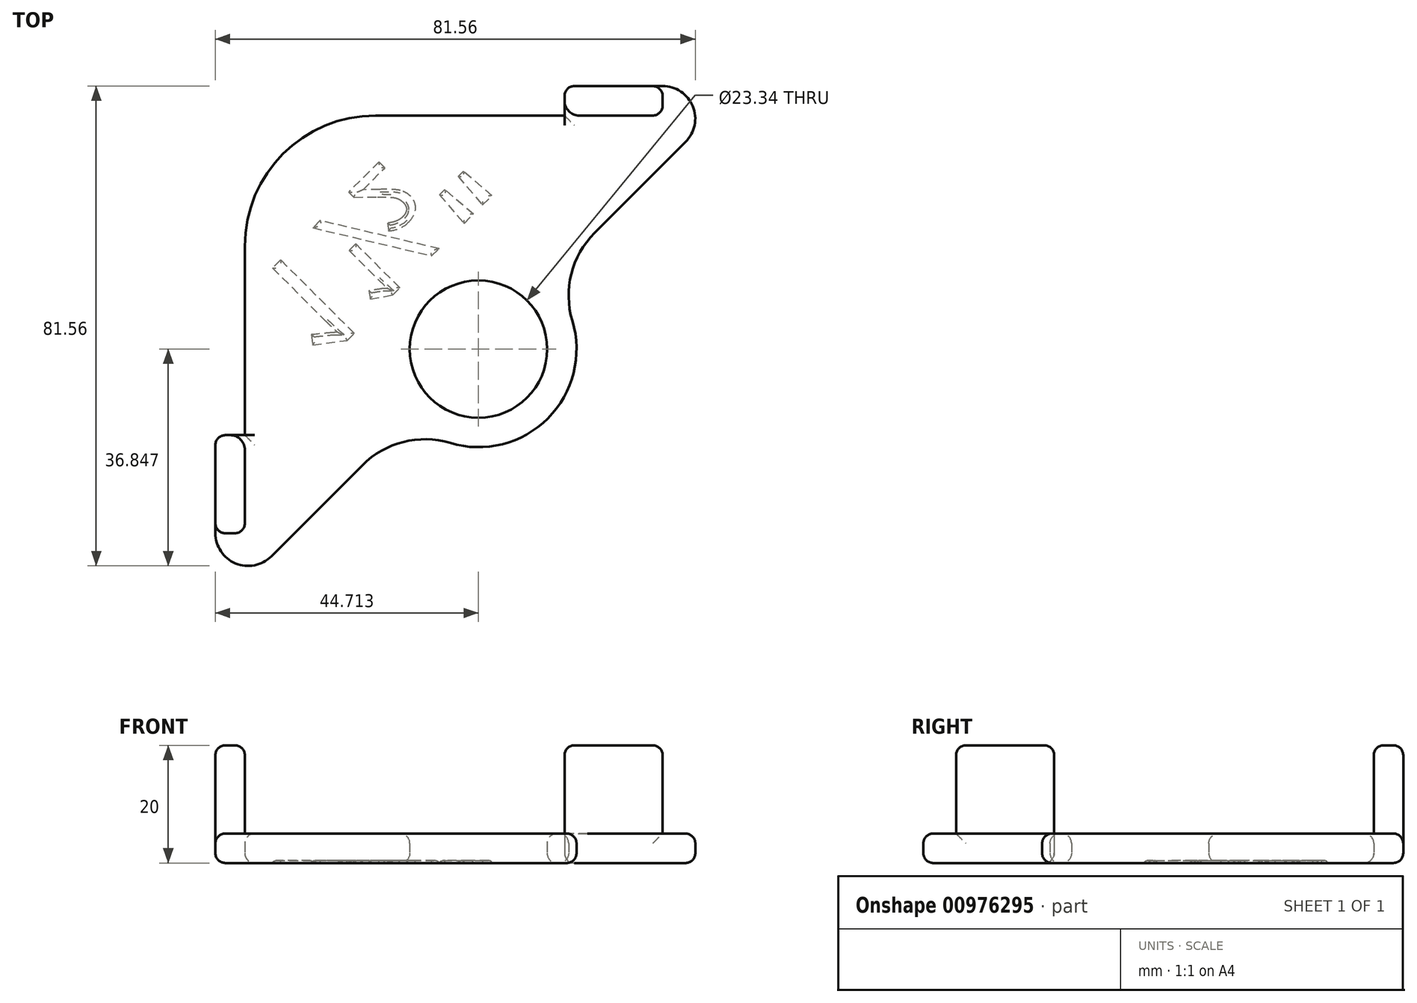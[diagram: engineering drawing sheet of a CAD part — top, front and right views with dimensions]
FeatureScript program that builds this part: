
annotation { "Feature Type Name" : "Feature", "Feature Type Description" : "" }
export const myFeature = defineFeature(function(context is Context, id is Id, definition is map)
    precondition{}
    {
        {
            assignVariable(context, id + "F0", {"name" : "t", "anyValue" : 5});
        }
        {
            var Q0;
            Q0=qCreatedBy(makeId("Top.planeOp"),FACE);
            var sketch = newSketch(context, id + "F1", { "sketchPlane" : qUnion([Q0])});
            skLineSegment(sketch, "E0", {"start": v(-22.22, 0) * mm, "end": v(-22.22, -48.78) * mm});
            skLineSegment(sketch, "E1", {"start": v(0, 22.22) * mm, "end": v(48.78, 22.22) * mm});
            skLineSegment(sketch, "E2", {"start": v(52.7, 17.74) * mm, "end": v(29.27, -5.7) * mm});
            skLineSegment(sketch, "E3.bottom", {"start": v(-22.22, -32.1) * mm, "end": v(-27.22, -32.1) * mm});
            skLineSegment(sketch, "E3.top", {"start": v(-22.22, -48.78) * mm, "end": v(-27.22, -48.78) * mm});
            skLineSegment(sketch, "E3.left", {"start": v(-22.22, -32.1) * mm, "end": v(-22.22, -48.78) * mm});
            skLineSegment(sketch, "E3.right", {"start": v(-27.22, -32.1) * mm, "end": v(-27.22, -48.78) * mm});
            skLineSegment(sketch, "E4.bottom", {"start": v(32.1, 22.22) * mm, "end": v(48.78, 22.22) * mm});
            skLineSegment(sketch, "E4.top", {"start": v(32.1, 27.22) * mm, "end": v(48.78, 27.22) * mm});
            skLineSegment(sketch, "E4.left", {"start": v(32.1, 22.22) * mm, "end": v(32.1, 27.22) * mm});
            skLineSegment(sketch, "E4.right", {"start": v(48.78, 22.22) * mm, "end": v(48.78, 27.22) * mm});
            skCircle(sketch, "E5", {"center": v(17.48, -17.48) * mm, "radius": 11.67 * mm});
            skArc(sketch, "E6", {"start": v(0, 22.22) * mm, "mid": v(-15.72, 15.72) * mm, "end": v(-22.22, 0) * mm});
            skArc(sketch, "E7", {"start": v(-22.22, 0) * mm, "mid": v(15.72, -15.72) * mm, "end": v(0, 22.22) * mm, "construction": true});
            skArc(sketch, "E8", {"start": v(29.27, -5.7) * mm, "mid": v(5.7, -5.7) * mm, "end": v(5.7, -29.27) * mm, "construction": true});
            skArc(sketch, "E9", {"start": v(5.7, -29.27) * mm, "mid": v(29.27, -29.27) * mm, "end": v(29.27, -5.7) * mm});
            skArc(sketch, "E10", {"start": v(48.78, 27.23) * mm, "mid": v(43.64, 19.54) * mm, "end": v(52.7, 17.74) * mm, "construction": true});
            skArc(sketch, "E11", {"start": v(52.7, 17.74) * mm, "mid": v(53.91, 23.8) * mm, "end": v(48.78, 27.23) * mm});
            skArc(sketch, "E12", {"start": v(-27.23, -48.78) * mm, "mid": v(-23.8, -53.91) * mm, "end": v(-17.74, -52.7) * mm});
            skArc(sketch, "E13", {"start": v(-17.74, -52.7) * mm, "mid": v(-19.54, -43.64) * mm, "end": v(-27.23, -48.78) * mm, "construction": true});
            skLineSegment(sketch, "E14", {"start": v(29.27, -5.7) * mm, "end": v(5.7, -29.27) * mm, "construction": true});
            skLineSegment(sketch, "E15", {"start": v(5.7, -29.27) * mm, "end": v(-17.74, -52.7) * mm});
            skSolve(sketch);
        }
        {
            var Q0;
            Q0=makeQuery(id+"F1.imprint","IMPRINT",FACE,{"disambiguationData":[TD([[makeQuery(id+"F1.imprint","IMPRINT",EDGE,{"derivedFrom":sQuery(id+"F1.wireOp",EDGE,"Bsdqljn9-m8OD-Z169-KwQe-wA3pNiIeevgB")}),1.0]])]});
            var Q1;
            Q1=makeQuery(id+"F1.imprint","IMPRINT",FACE,{"disambiguationData":[TD([[makeQuery(id+"F1.imprint","IMPRINT",EDGE,{"derivedFrom":sQuery(id+"F1.wireOp",EDGE,"E2")}),-1.0]])]});
            var Q2;
            Q2=makeQuery(id+"F1.imprint","IMPRINT",FACE,{"disambiguationData":[TD([[makeQuery(id+"F1.imprint","IMPRINT",EDGE,{"derivedFrom":sQuery(id+"F1.wireOp",EDGE,"E2")}),-1.0]])]});
            var Q3;
            {var subQ0=sQuery(id+"F1.wireOp",EDGE,"1yZtRJ6P-QjRJ-GIre-H2JQ-c21tXZH1Mfqz");var subQ1=makeQuery(id+"F1.imprint","INTERSECT",VERTEX,{"derivedFrom":[subQ0,sQuery(id+"F1.wireOp",EDGE,"E0")]});Q3=makeQuery(id+"F1.imprint","IMPRINT",FACE,{"disambiguationData":[TD([[makeQuery(id+"F1.imprint","IMPRINT",EDGE,{"disambiguationData":[TD([[subQ1,1.0]])],"derivedFrom":subQ0}),1.0]])]});}
            var Q4;
            {var subQ0=sQuery(id+"F1.wireOp",EDGE,"sP8yukeB-kcOP-x4iM-DJbK-dVnLuw5eq7dv");var subQ1=sQuery(id+"F1.wireOp",EDGE,"1yZtRJ6P-QjRJ-GIre-H2JQ-c21tXZH1Mfqz");var subQ2=makeQuery(id+"F1.imprint","INTERSECT",VERTEX,{"disambiguationData":[OD(0.0)],"derivedFrom":[subQ1,subQ0]});Q4=makeQuery(id+"F1.imprint","IMPRINT",FACE,{"disambiguationData":[TD([[makeQuery(id+"F1.imprint","IMPRINT",EDGE,{"disambiguationData":[TD([[subQ2,-1.0]])],"derivedFrom":subQ1}),1.0]])]});}
            var Q5;
            {var subQ0=sQuery(id+"F1.wireOp",EDGE,"sP8yukeB-kcOP-x4iM-DJbK-dVnLuw5eq7dv");var subQ1=sQuery(id+"F1.wireOp",EDGE,"1yZtRJ6P-QjRJ-GIre-H2JQ-c21tXZH1Mfqz");var subQ2=makeQuery(id+"F1.imprint","INTERSECT",VERTEX,{"disambiguationData":[OD(0.0)],"derivedFrom":[subQ1,subQ0]});Q5=makeQuery(id+"F1.imprint","IMPRINT",FACE,{"disambiguationData":[TD([[makeQuery(id+"F1.imprint","IMPRINT",EDGE,{"disambiguationData":[TD([[subQ2,-1.0]])],"derivedFrom":subQ1}),-1.0]])]});}
            var Q6;
            {var subQ0=sQuery(id+"F1.wireOp",EDGE,"E2");var subQ1=sQuery(id+"F1.wireOp",EDGE,"1yZtRJ6P-QjRJ-GIre-H2JQ-c21tXZH1Mfqz");var subQ2=makeQuery(id+"F1.imprint","INTERSECT",VERTEX,{"disambiguationData":[OD(1.0)],"derivedFrom":[subQ1,subQ0]});Q6=makeQuery(id+"F1.imprint","IMPRINT",FACE,{"disambiguationData":[TD([[makeQuery(id+"F1.imprint","IMPRINT",EDGE,{"disambiguationData":[TD([[subQ2,-1.0]])],"derivedFrom":subQ1}),-1.0]])]});}
            var Q7;
            Q7=makeQuery(id+"F1.imprint","IMPRINT",FACE,{"disambiguationData":[TD([[makeQuery(id+"F1.imprint","IMPRINT",EDGE,{"derivedFrom":sQuery(id+"F1.wireOp",EDGE,"E2")}),-1.0]])]});
            var Q8;
            Q8=makeQuery(id+"F1.imprint","IMPRINT",FACE,{"disambiguationData":[TD([[makeQuery(id+"F1.imprint","IMPRINT",EDGE,{"derivedFrom":sQuery(id+"F1.wireOp",EDGE,"E2")}),-1.0]])]});
            var Q9;
            {var subQ0=sQuery(id+"F1.wireOp",EDGE,"E2");var subQ1=sQuery(id+"F1.wireOp",EDGE,"sP8yukeB-kcOP-x4iM-DJbK-dVnLuw5eq7dv");var subQ2=makeQuery(id+"F1.imprint","INTERSECT",VERTEX,{"disambiguationData":[OD(0.0)],"derivedFrom":[subQ1,subQ0]});Q9=makeQuery(id+"F1.imprint","IMPRINT",FACE,{"disambiguationData":[TD([[makeQuery(id+"F1.imprint","IMPRINT",EDGE,{"disambiguationData":[TD([[subQ2,1.0]])],"derivedFrom":subQ1}),1.0]])]});}
            extrude(context, id + "F2", {"entities" : qUnion([Q0, Q1, Q2, Q3, Q4, Q5, Q6, Q7, Q8, Q9]), "depth" : (getVariable(context, 't')) * mm, "offsetDistance" : 25 * mm});
        }
        {
            var Q0;
            Q0=makeQuery(id+"F2.opExtrude","CAP_FACE",FACE,{"disambiguationData":[OSD([sQuery(id+"F1.wireOp",EDGE,"E0"),sQuery(id+"F1.wireOp",EDGE,"E1"),sQuery(id+"F1.wireOp",EDGE,"E2"),sQuery(id+"F1.wireOp",EDGE,"E3.top"),sQuery(id+"F1.wireOp",EDGE,"E4.right"),sQuery(id+"F1.wireOp",EDGE,"E5"),sQuery(id+"F1.wireOp",EDGE,"E6"),sQuery(id+"F1.wireOp",EDGE,"E9"),sQuery(id+"F1.wireOp",EDGE,"E11"),sQuery(id+"F1.wireOp",EDGE,"E12"),sQuery(id+"F1.wireOp",EDGE,"E15")])],"isStart":true});
            var sketch = newSketch(context, id + "F3", { "sketchPlane" : qUnion([Q0])});
            skText(sketch, "E16", { "text": "1½\"", "fontName": "OpenSans-Regular.ttf"});
            const initialGuessF3  = {"E16": [-0.02222, 0.00843, 0.7071, -0.7071, 0.01781]};
            skSetInitialGuess(sketch, initialGuessF3);
            skSolve(sketch);
        }
        {
            var Q0;
            {var subQ2=sQuery(id+"F1.wireOp",EDGE,"E3.bottom");Q0=makeQuery(id+"F1.imprint","IMPRINT",FACE,{"disambiguationData":[TD([[makeQuery(id+"F1.imprint","IMPRINT",EDGE,{"derivedFrom":subQ2}),1.0]])]});}
            var Q1;
            {var subQ2=sQuery(id+"F1.wireOp",EDGE,"E3.bottom");Q1=makeQuery(id+"F1.imprint","IMPRINT",FACE,{"disambiguationData":[TD([[makeQuery(id+"F1.imprint","IMPRINT",EDGE,{"derivedFrom":subQ2}),1.0]])]});}
            var Q2;
            Q2=makeQuery(id+"F1.imprint","IMPRINT",FACE,{"disambiguationData":[TD([[makeQuery(id+"F1.imprint","IMPRINT",EDGE,{"derivedFrom":sQuery(id+"F1.wireOp",EDGE,"E4.top")}),-1.0]])]});
            var Q3;
            Q3=makeQuery(id+"F1.imprint","IMPRINT",FACE,{"disambiguationData":[TD([[makeQuery(id+"F1.imprint","IMPRINT",EDGE,{"derivedFrom":sQuery(id+"F1.wireOp",EDGE,"E4.top")}),-1.0]])]});
            extrude(context, id + "F4", {"entities" : qUnion([Q0, Q1, Q2, Q3]), "operationType" : NewBodyOperationType.ADD, "depth" : (15 + getVariable(context, 't')) * mm, "offsetDistance" : 25 * mm});
        }
        {
            var Q0;
            Q0=makeQuery(id+"F2.opExtrude","SWEPT_EDGE",EDGE,{"disambiguationData":[OSD([sQuery(id+"F1.wireOp",EDGE,"E2"),sQuery(id+"F1.wireOp",EDGE,"E9")])]});
            var Q1;
            Q1=makeQuery(id+"F2.opExtrude","SWEPT_EDGE",EDGE,{"disambiguationData":[OSD([sQuery(id+"F1.wireOp",EDGE,"E9"),sQuery(id+"F1.wireOp",EDGE,"E15")])]});
            fillet(context, id + "F5", {"entities" : qUnion([Q0, Q1]), "radius" : 15 * mm, "tangentPropagation" : true, "allowEdgeOverflow" : false});
        }
        {
            var Q0;
            {var subQ0=sQuery(id+"F1.wireOp",EDGE,"E0");var subQ1=sQuery(id+"F1.wireOp",EDGE,"E3.bottom");Q0=makeQuery(id+"F4.boolean.opBoolean","SPLIT",EDGE,{"disambiguationData":[topologyDisambiguationEdgeConnected([makeQuery(id+"F2.opExtrude","SWEPT_FACE",FACE,{"disambiguationData":[OSD([subQ0])]})])],"derivedFrom":makeQuery(id+"F4.opExtrude","SWEPT_EDGE",EDGE,{"disambiguationData":[OSD([subQ0,subQ1])]})});}
            var Q1;
            {var subQ0=sQuery(id+"F1.wireOp",EDGE,"E1");var subQ1=sQuery(id+"F1.wireOp",EDGE,"E4.left");Q1=makeQuery(id+"F4.boolean.opBoolean","SPLIT",EDGE,{"disambiguationData":[topologyDisambiguationEdgeConnected([makeQuery(id+"F2.opExtrude","SWEPT_FACE",FACE,{"disambiguationData":[OSD([subQ0])]})])],"derivedFrom":makeQuery(id+"F4.opExtrude","SWEPT_EDGE",EDGE,{"disambiguationData":[OSD([subQ0,subQ1])]})});}
            var Q2;
            Q2=makeQuery(id+"F2.opExtrude","CAP_EDGE",EDGE,{"disambiguationData":[OSD([sQuery(id+"F1.wireOp",EDGE,"E3.top")])],"isStart":false});
            var Q3;
            Q3=makeQuery(id+"F2.opExtrude","CAP_EDGE",EDGE,{"disambiguationData":[OSD([sQuery(id+"F1.wireOp",EDGE,"E4.right")])],"isStart":false});
            fillet(context, id + "F6", {"entities" : qUnion([Q0, Q1, Q2, Q3]), "radius" : (getVariable(context, 't') / 2) * mm, "tangentPropagation" : true, "allowEdgeOverflow" : false});
        }
        {
            var Q0;
            Q0=makeQuery(id+"F4.boolean.opBoolean","SPLIT",EDGE,{"derivedFrom":makeQuery(id+"F4.opExtrude","SWEPT_EDGE",EDGE,{"disambiguationData":[OSD([sQuery(id+"F1.wireOp",EDGE,"E4.top"),sQuery(id+"F1.wireOp",EDGE,"E4.right"),sQuery(id+"F1.wireOp",EDGE,"E11")])]})});
            var Q1;
            Q1=makeQuery(id+"F4.opExtrude","SWEPT_EDGE",EDGE,{"disambiguationData":[OSD([sQuery(id+"F1.wireOp",EDGE,"E1"),sQuery(id+"F1.wireOp",EDGE,"E4.right")])]});
            var Q2;
            {var subQ0=sQuery(id+"F1.wireOp",EDGE,"E1");var subQ1=sQuery(id+"F1.wireOp",EDGE,"E4.left");Q2=makeQuery(id+"F4.boolean.opBoolean","SPLIT",EDGE,{"disambiguationData":[topologyDisambiguationEdgeConnected([makeQuery(id+"F4.opExtrude","SWEPT_FACE",FACE,{"disambiguationData":[OSD([subQ0])]})])],"derivedFrom":makeQuery(id+"F4.opExtrude","SWEPT_EDGE",EDGE,{"disambiguationData":[OSD([subQ0,subQ1])]})});}
            var Q3;
            Q3=makeQuery(id+"F4.opExtrude","CAP_FACE",FACE,{"disambiguationData":[OSD([sQuery(id+"F1.wireOp",EDGE,"E1"),sQuery(id+"F1.wireOp",EDGE,"E4.top"),sQuery(id+"F1.wireOp",EDGE,"E4.left"),sQuery(id+"F1.wireOp",EDGE,"E4.right")])],"isStart":false});
            var Q4;
            Q4=makeQuery(id+"F4.opExtrude","CAP_FACE",FACE,{"disambiguationData":[OSD([sQuery(id+"F1.wireOp",EDGE,"E0"),sQuery(id+"F1.wireOp",EDGE,"E3.bottom"),sQuery(id+"F1.wireOp",EDGE,"E3.top"),sQuery(id+"F1.wireOp",EDGE,"E3.right")])],"isStart":false});
            var Q5;
            Q5=makeQuery(id+"F4.boolean.opBoolean","SPLIT",EDGE,{"derivedFrom":makeQuery(id+"F4.opExtrude","SWEPT_EDGE",EDGE,{"disambiguationData":[OSD([sQuery(id+"F1.wireOp",EDGE,"E3.top"),sQuery(id+"F1.wireOp",EDGE,"E3.right"),sQuery(id+"F1.wireOp",EDGE,"E12")])]})});
            var Q6;
            Q6=makeQuery(id+"F4.opExtrude","SWEPT_EDGE",EDGE,{"disambiguationData":[OSD([sQuery(id+"F1.wireOp",EDGE,"E0"),sQuery(id+"F1.wireOp",EDGE,"E3.top")])]});
            var Q7;
            {var subQ0=sQuery(id+"F1.wireOp",EDGE,"E0");var subQ1=sQuery(id+"F1.wireOp",EDGE,"E3.bottom");Q7=makeQuery(id+"F4.boolean.opBoolean","SPLIT",EDGE,{"disambiguationData":[topologyDisambiguationEdgeConnected([makeQuery(id+"F4.opExtrude","SWEPT_FACE",FACE,{"disambiguationData":[OSD([subQ0])]})])],"derivedFrom":makeQuery(id+"F4.opExtrude","SWEPT_EDGE",EDGE,{"disambiguationData":[OSD([subQ0,subQ1])]})});}
            var Q8;
            {var subQ0=sQuery(id+"F1.wireOp",EDGE,"E4.bottom");var subQ1=sQuery(id+"F1.wireOp",EDGE,"E1");var subQ2=sQuery(id+"F1.wireOp",EDGE,"E4.left");Q8=makeQuery(id+"F6.opFillet","BLEND_EDGE",EDGE,{"blendedFrom":[makeQuery(id+"F4.boolean.opBoolean","SPLIT",EDGE,{"disambiguationData":[topologyDisambiguationEdgeConnected([makeQuery(id+"F2.opExtrude","SWEPT_FACE",FACE,{"disambiguationData":[OSD([subQ1,subQ0])]})])],"derivedFrom":makeQuery(id+"F4.opExtrude","SWEPT_EDGE",EDGE,{"disambiguationData":[OSD([subQ1,subQ0,subQ2])]})}),makeQuery(id+"F4.opExtrude","SWEPT_FACE",FACE,{"disambiguationData":[OSD([sQuery(id+"F1.wireOp",EDGE,"E4.top")])]})],"blendedInto":[makeQuery(id+"F4.opExtrude","SWEPT_FACE",FACE,{"disambiguationData":[OSD([sQuery(id+"F1.wireOp",EDGE,"E4.top")])]})]});}
            var Q9;
            {var subQ0=sQuery(id+"F1.wireOp",EDGE,"E3.left");var subQ1=sQuery(id+"F1.wireOp",EDGE,"E0");var subQ2=sQuery(id+"F1.wireOp",EDGE,"E3.bottom");Q9=makeQuery(id+"F6.opFillet","BLEND_EDGE",EDGE,{"blendedFrom":[makeQuery(id+"F4.boolean.opBoolean","SPLIT",EDGE,{"disambiguationData":[topologyDisambiguationEdgeConnected([makeQuery(id+"F2.opExtrude","SWEPT_FACE",FACE,{"disambiguationData":[OSD([subQ1,subQ0])]})])],"derivedFrom":makeQuery(id+"F4.opExtrude","SWEPT_EDGE",EDGE,{"disambiguationData":[OSD([subQ1,subQ2,subQ0])]})}),makeQuery(id+"F4.opExtrude","SWEPT_FACE",FACE,{"disambiguationData":[OSD([sQuery(id+"F1.wireOp",EDGE,"E3.right")])]})],"blendedInto":[makeQuery(id+"F4.opExtrude","SWEPT_FACE",FACE,{"disambiguationData":[OSD([sQuery(id+"F1.wireOp",EDGE,"E3.right")])]})]});}
            var Q10;
            Q10=makeQuery(id+"F4.opExtrude","SWEPT_EDGE",EDGE,{"disambiguationData":[OSD([sQuery(id+"F1.wireOp",EDGE,"E4.top"),sQuery(id+"F1.wireOp",EDGE,"E4.left")])]});
            var Q11;
            Q11=makeQuery(id+"F4.opExtrude","SWEPT_EDGE",EDGE,{"disambiguationData":[OSD([sQuery(id+"F1.wireOp",EDGE,"E3.bottom"),sQuery(id+"F1.wireOp",EDGE,"E3.right")])]});
            var Q12;
            Q12=makeQuery(id+"F6.opFillet","BLEND_EDGE",EDGE,{"blendedFrom":[makeQuery(id+"F2.opExtrude","CAP_EDGE",EDGE,{"disambiguationData":[OSD([sQuery(id+"F1.wireOp",EDGE,"E3.top")])],"isStart":false}),makeQuery(id+"F4.opExtrude","SWEPT_FACE",FACE,{"disambiguationData":[OSD([sQuery(id+"F1.wireOp",EDGE,"E0")])]})],"blendedInto":[makeQuery(id+"F4.opExtrude","SWEPT_FACE",FACE,{"disambiguationData":[OSD([sQuery(id+"F1.wireOp",EDGE,"E0")])]})]});
            var Q13;
            Q13=makeQuery(id+"F6.opFillet","BLEND_EDGE",EDGE,{"blendedFrom":[makeQuery(id+"F2.opExtrude","CAP_EDGE",EDGE,{"disambiguationData":[OSD([sQuery(id+"F1.wireOp",EDGE,"E4.right")])],"isStart":false}),makeQuery(id+"F4.opExtrude","SWEPT_FACE",FACE,{"disambiguationData":[OSD([sQuery(id+"F1.wireOp",EDGE,"E1")])]})],"blendedInto":[makeQuery(id+"F4.opExtrude","SWEPT_FACE",FACE,{"disambiguationData":[OSD([sQuery(id+"F1.wireOp",EDGE,"E1")])]})]});
            fillet(context, id + "F7", {"entities" : qUnion([Q0, Q1, Q2, Q3, Q4, Q5, Q6, Q7, Q8, Q9, Q10, Q11, Q12, Q13]), "radius" : (getVariable(context, 't') / 3) * mm, "allowEdgeOverflow" : false});
        }
        {
            var Q0;
            Q0=makeQuery(id+"F2.opExtrude","SWEPT_FACE",FACE,{"disambiguationData":[OSD([sQuery(id+"F1.wireOp",EDGE,"E5")])]});
            var Q1;
            {var subQ0=sQuery(id+"F1.wireOp",EDGE,"E4.right");var subQ1=sQuery(id+"F1.wireOp",EDGE,"E1");var subQ2=sQuery(id+"F1.wireOp",EDGE,"E3.top");var subQ3=sQuery(id+"F1.wireOp",EDGE,"E0");Q1=makeQuery(id+"F4.boolean.opBoolean","MERGE",FACE,{"derivedFrom":[makeQuery(id+"F2.opExtrude","CAP_FACE",FACE,{"disambiguationData":[OSD([subQ3,subQ1,sQuery(id+"F1.wireOp",EDGE,"E2"),subQ2,subQ0,sQuery(id+"F1.wireOp",EDGE,"E5"),sQuery(id+"F1.wireOp",EDGE,"E6"),sQuery(id+"F1.wireOp",EDGE,"E9"),sQuery(id+"F1.wireOp",EDGE,"E11"),sQuery(id+"F1.wireOp",EDGE,"E12"),sQuery(id+"F1.wireOp",EDGE,"E15")])],"isStart":true}),makeQuery(id+"F4.opExtrude","CAP_FACE",FACE,{"disambiguationData":[OSD([subQ3,sQuery(id+"F1.wireOp",EDGE,"E3.bottom"),subQ2,sQuery(id+"F1.wireOp",EDGE,"E3.right")])],"isStart":true}),makeQuery(id+"F4.opExtrude","CAP_FACE",FACE,{"disambiguationData":[OSD([subQ1,sQuery(id+"F1.wireOp",EDGE,"E4.top"),sQuery(id+"F1.wireOp",EDGE,"E4.left"),subQ0])],"isStart":true})]});}
            var Q2;
            Q2=makeQuery(id+"F2.opExtrude","CAP_EDGE",EDGE,{"disambiguationData":[OSD([sQuery(id+"F1.wireOp",EDGE,"E2")])],"isStart":false});
            var Q3;
            {var subQ0=sQuery(id+"F1.wireOp",EDGE,"E1");Q3=makeQuery(id+"F4.boolean.opBoolean","SPLIT",EDGE,{"disambiguationData":[topologyDisambiguationEdgeConnected([makeQuery(id+"F2.opExtrude","SWEPT_FACE",FACE,{"disambiguationData":[OSD([subQ0])]})])],"derivedFrom":makeQuery(id+"F2.opExtrude","CAP_EDGE",EDGE,{"disambiguationData":[OSD([subQ0])],"isStart":false})});}
            fillet(context, id + "F8", {"entities" : qUnion([Q0, Q1, Q2, Q3]), "radius" : (getVariable(context, 't') / 3) * mm, "tangentPropagation" : true, "allowEdgeOverflow" : false});
        }
        {
            var Q0;
            Q0=makeQuery(id+"F3.imprint","IMPRINT",FACE,{"disambiguationData":[TD([[makeQuery(id+"F3.imprint","IMPRINT",EDGE,{"derivedFrom":sQuery(id+"F3.wireOp",EDGE,"E16.sketch_text.stroke-40")}),-1.0]])]});
            var Q1;
            Q1=makeQuery(id+"F3.imprint","IMPRINT",FACE,{"disambiguationData":[TD([[makeQuery(id+"F3.imprint","IMPRINT",EDGE,{"derivedFrom":sQuery(id+"F3.wireOp",EDGE,"E16.sketch_text.stroke-36")}),-1.0]])]});
            var Q2;
            Q2=makeQuery(id+"F3.imprint","IMPRINT",FACE,{"disambiguationData":[TD([[makeQuery(id+"F3.imprint","IMPRINT",EDGE,{"derivedFrom":sQuery(id+"F3.wireOp",EDGE,"E16.sketch_text.stroke-17")}),-1.0]])]});
            var Q3;
            Q3=makeQuery(id+"F3.imprint","IMPRINT",FACE,{"disambiguationData":[TD([[makeQuery(id+"F3.imprint","IMPRINT",EDGE,{"derivedFrom":sQuery(id+"F3.wireOp",EDGE,"E16.sketch_text.stroke-9")}),-1.0]])]});
            var Q4;
            Q4=makeQuery(id+"F3.imprint","IMPRINT",FACE,{"disambiguationData":[TD([[makeQuery(id+"F3.imprint","IMPRINT",EDGE,{"derivedFrom":sQuery(id+"F3.wireOp",EDGE,"E16.sketch_text.stroke-0")}),-1.0]])]});
            var Q5;
            Q5=makeQuery(id+"F3.imprint","IMPRINT",FACE,{"disambiguationData":[TD([[makeQuery(id+"F3.imprint","IMPRINT",EDGE,{"derivedFrom":sQuery(id+"F3.wireOp",EDGE,"E16.sketch_text.stroke-41")}),-1.0]])]});
            var Q6;
            Q6=makeQuery(id+"F3.imprint","IMPRINT",FACE,{"disambiguationData":[TD([[makeQuery(id+"F3.imprint","IMPRINT",EDGE,{"derivedFrom":sQuery(id+"F3.wireOp",EDGE,"E16.sketch_text.stroke-45")}),-1.0]])]});
            extrude(context, id + "F9", {"entities" : qUnion([Q0, Q1, Q2, Q3, Q4, Q5, Q6]), "operationType" : NewBodyOperationType.REMOVE, "oppositeDirection" : true, "depth" : .4 * mm, "offsetDistance" : 25 * mm});
        }
        {
            var Q0;
            Q0=makeQuery(id+"F9.boolean.opBoolean","COPY",FACE,{"derivedFrom":makeQuery(id+"F9.opExtrude","CAP_FACE",FACE,{"disambiguationData":[OSD([sQuery(id+"F3.wireOp",EDGE,"E16.sketch_text.stroke-0"),sQuery(id+"F3.wireOp",EDGE,"E16.sketch_text.stroke-1"),sQuery(id+"F3.wireOp",EDGE,"E16.sketch_text.stroke-2"),sQuery(id+"F3.wireOp",EDGE,"E16.sketch_text.stroke-3"),sQuery(id+"F3.wireOp",EDGE,"E16.sketch_text.stroke-4"),sQuery(id+"F3.wireOp",EDGE,"E16.sketch_text.stroke-5"),sQuery(id+"F3.wireOp",EDGE,"E16.sketch_text.stroke-6"),sQuery(id+"F3.wireOp",EDGE,"E16.sketch_text.stroke-7"),sQuery(id+"F3.wireOp",EDGE,"E16.sketch_text.stroke-8")])],"isStart":false})});
            var Q1;
            Q1=makeQuery(id+"F9.boolean.opBoolean","COPY",FACE,{"derivedFrom":makeQuery(id+"F9.opExtrude","CAP_FACE",FACE,{"disambiguationData":[OSD([sQuery(id+"F3.wireOp",EDGE,"E16.sketch_text.stroke-17"),sQuery(id+"F3.wireOp",EDGE,"E16.sketch_text.stroke-18"),sQuery(id+"F3.wireOp",EDGE,"E16.sketch_text.stroke-19"),sQuery(id+"F3.wireOp",EDGE,"E16.sketch_text.stroke-20"),sQuery(id+"F3.wireOp",EDGE,"E16.sketch_text.stroke-21"),sQuery(id+"F3.wireOp",EDGE,"E16.sketch_text.stroke-22"),sQuery(id+"F3.wireOp",EDGE,"E16.sketch_text.stroke-23"),sQuery(id+"F3.wireOp",EDGE,"E16.sketch_text.stroke-24"),sQuery(id+"F3.wireOp",EDGE,"E16.sketch_text.stroke-25"),sQuery(id+"F3.wireOp",EDGE,"E16.sketch_text.stroke-26"),sQuery(id+"F3.wireOp",EDGE,"E16.sketch_text.stroke-27"),sQuery(id+"F3.wireOp",EDGE,"E16.sketch_text.stroke-28"),sQuery(id+"F3.wireOp",EDGE,"E16.sketch_text.stroke-29"),sQuery(id+"F3.wireOp",EDGE,"E16.sketch_text.stroke-30"),sQuery(id+"F3.wireOp",EDGE,"E16.sketch_text.stroke-31"),sQuery(id+"F3.wireOp",EDGE,"E16.sketch_text.stroke-32"),sQuery(id+"F3.wireOp",EDGE,"E16.sketch_text.stroke-33"),sQuery(id+"F3.wireOp",EDGE,"E16.sketch_text.stroke-34"),sQuery(id+"F3.wireOp",EDGE,"E16.sketch_text.stroke-35")])],"isStart":false})});
            var Q2;
            Q2=makeQuery(id+"F9.boolean.opBoolean","COPY",FACE,{"derivedFrom":makeQuery(id+"F9.opExtrude","CAP_FACE",FACE,{"disambiguationData":[OSD([sQuery(id+"F3.wireOp",EDGE,"E16.sketch_text.stroke-9"),sQuery(id+"F3.wireOp",EDGE,"E16.sketch_text.stroke-10"),sQuery(id+"F3.wireOp",EDGE,"E16.sketch_text.stroke-11"),sQuery(id+"F3.wireOp",EDGE,"E16.sketch_text.stroke-12"),sQuery(id+"F3.wireOp",EDGE,"E16.sketch_text.stroke-13"),sQuery(id+"F3.wireOp",EDGE,"E16.sketch_text.stroke-14"),sQuery(id+"F3.wireOp",EDGE,"E16.sketch_text.stroke-15"),sQuery(id+"F3.wireOp",EDGE,"E16.sketch_text.stroke-16")])],"isStart":false})});
            var Q3;
            Q3=makeQuery(id+"F9.boolean.opBoolean","COPY",FACE,{"derivedFrom":makeQuery(id+"F9.opExtrude","CAP_FACE",FACE,{"disambiguationData":[OSD([sQuery(id+"F3.wireOp",EDGE,"E16.sketch_text.stroke-36"),sQuery(id+"F3.wireOp",EDGE,"E16.sketch_text.stroke-37"),sQuery(id+"F3.wireOp",EDGE,"E16.sketch_text.stroke-38"),sQuery(id+"F3.wireOp",EDGE,"E16.sketch_text.stroke-39")])],"isStart":false})});
            var Q4;
            Q4=makeQuery(id+"F9.boolean.opBoolean","COPY",FACE,{"derivedFrom":makeQuery(id+"F9.opExtrude","CAP_FACE",FACE,{"disambiguationData":[OSD([sQuery(id+"F3.wireOp",EDGE,"E16.sketch_text.stroke-40"),sQuery(id+"F3.wireOp",EDGE,"E16.sketch_text.stroke-41"),sQuery(id+"F3.wireOp",EDGE,"E16.sketch_text.stroke-42"),sQuery(id+"F3.wireOp",EDGE,"E16.sketch_text.stroke-43")])],"isStart":false})});
            var Q5;
            Q5=makeQuery(id+"F9.boolean.opBoolean","COPY",FACE,{"derivedFrom":makeQuery(id+"F9.opExtrude","CAP_FACE",FACE,{"disambiguationData":[OSD([sQuery(id+"F3.wireOp",EDGE,"E16.sketch_text.stroke-13"),sQuery(id+"F3.wireOp",EDGE,"E16.sketch_text.stroke-14"),sQuery(id+"F3.wireOp",EDGE,"E16.sketch_text.stroke-15"),sQuery(id+"F3.wireOp",EDGE,"E16.sketch_text.stroke-16"),sQuery(id+"F3.wireOp",EDGE,"E16.sketch_text.stroke-17"),sQuery(id+"F3.wireOp",EDGE,"E16.sketch_text.stroke-18"),sQuery(id+"F3.wireOp",EDGE,"E16.sketch_text.stroke-19"),sQuery(id+"F3.wireOp",EDGE,"E16.sketch_text.stroke-20"),sQuery(id+"F3.wireOp",EDGE,"E16.sketch_text.stroke-21")])],"isStart":false})});
            var Q6;
            Q6=makeQuery(id+"F9.boolean.opBoolean","COPY",FACE,{"derivedFrom":makeQuery(id+"F9.opExtrude","CAP_FACE",FACE,{"disambiguationData":[OSD([sQuery(id+"F3.wireOp",EDGE,"E16.sketch_text.stroke-45"),sQuery(id+"F3.wireOp",EDGE,"E16.sketch_text.stroke-46"),sQuery(id+"F3.wireOp",EDGE,"E16.sketch_text.stroke-47"),sQuery(id+"F3.wireOp",EDGE,"E16.sketch_text.stroke-48")])],"isStart":false})});
            fillet(context, id + "F10", {"entities" : qUnion([Q0, Q1, Q2, Q3, Q4, Q5, Q6]), "radius" : .4 * mm, "tangentPropagation" : true, "allowEdgeOverflow" : false});
        }
    });
